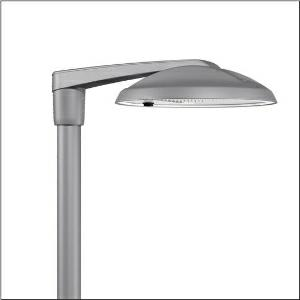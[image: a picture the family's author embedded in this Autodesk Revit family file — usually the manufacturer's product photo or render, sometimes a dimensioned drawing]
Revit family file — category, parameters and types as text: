
# Revit family: dl_r__50_iq_mini___st1_0a_5xa248d31u08ne_2837
name_source: partatom
category: Lighting Fixtures
units: mm (PartAtom-declared; Revit-internal decimal feet)

## family parameters
Cut with Voids When Loaded = No
Host = Face
Light Source = No
Part Type = Normal
Room Calculation Point = No
Round Connector Dimension = Use Diameter
Shared = No

## types (1)
- --- (1 x LED, 17900 lm, 110.1 W, 3000K)
    Apparent Load = 110 VA
    CIE Flux Codes = 37 72 97 100 100
    Color Rendering = 70
    Color Temperature = 3000K
    Default Elevation = 1800 mm
    Description = DL® 50 iQ mini, mast luminaire, primary light control with lens, of PMMA, primary optical cover: cover, of toughened safety glass, transparent, light distribution: ST1.0a, light emission: direct distribution, primary light characteristic: asymmetric, installation type: post-top, side-entry, LED, High Power LED, rated luminous flux: 17.900lm, luminous efficacy: 163lm/W, light colour: 730, colour temperature: 3000K, control gear: iQ-Street Remote, D4i with power reduction, control: optimised constant luminous flux control (CLO 2.0), Desk-Remote (wireless, voltage-free reading and setting of iQ features in the workshop via application-optimized NFC function/RFID function), Light-Fading, Smart-Wire, Night-Set, Lumen-Switch, Temp-Guard, Auto-Match, Street-Remote, pre-setting: logarithmic dimming characteristic, mains connection: 220..240V, AC, 50/60Hz, connection cable pre-assembled, cable length: 10,5m, start of lifetime: 110W, end of service life: 116W, reduction: 50W, luminaire housing, of diecast aluminium, powder-coated, Siteco® metallic grey (DB 702S), inclination adjustable: 0°, 5°, 10° (post-top) | 0°, -5°, -10°, -15° (side-entry), please order mast post-top element or mast side-entry element separately, diameter: 500mm, height: 115mm, post-top: for spigot size d x l = 76 x 100mm; with reducer (optional accessory) 60 x 100mm | side-entry: for spigot size d x l = 60 x 100mm; with reducer (optional accessory) 42 x 100mm, mounting height: 4..6m, Smart Interface below, protection rating (complete): IP66, insulation class (complete): insulation class II (safety insulation), certification: CE, ENEC, ENEC+, VDE, impact resistance: IK08, permissible operating ambient temperature for outdoor applications: -25..+40°C, standard-compliant lighting for roads and squares, packaging unit: 1 piece

Light Distribution: ST1.0a
    Height = 115 mm
    Lamp = 1 x LED
    Lamp Light Flux = 17900 lm
    Lamp Power = 110.1 W
    Lamp count = 1
    Length = 500 mm
    Luminous efficacy = 163 lm/W
    Manufacturer = Siteco
    ModVariant = No
    Model = 5XA248D31U08NE
    Number of Poles = 1
    OnlyDefault = Yes
    Power Factor = 1
    Product Name = DL® 50 iQ mini | ST1.0a
    Product group = mast luminaire | pylon top
    ProductGroupID = 6100
    Protection Class = Protection class II
    Protection Degree = IP 66
    RLX_Detail_Level = 1
    RLX_Emergency_Light_Flux = 0 lm
    RLX_Emergency_Type = 0
    RLX_Emergency_Type_DB = No
    RlxData = <blob elided: 107325 chars, md5=e1686bcd>
    Socket = socket
    Standby Power = 0 W
    System Light Flux = 17900 lm
    System Power = 110 W
    Type Comments = factory setting: luminous flux: 100 % | dim-lin: 254 | 601 mA
    Type Image = l_1296955.jpg
    URL = http://relux.com
    VarID = @adj_065438
    Voltage = 0 V
    Weight = 0.00 kg
    Width = 0 mm  [stored 0 ft]

note: [stored X ft] marks values corroborated as IEEE doubles in the binary element streams (Revit-internal decimal feet)

## geometry (parser evidence)
native form markers: Blend x4, Sweep x10
no freeform markers — native parametric forms only
